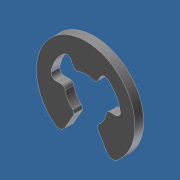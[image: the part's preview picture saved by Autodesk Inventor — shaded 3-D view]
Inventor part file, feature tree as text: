
AUTODESK INVENTOR PART (.ipt)
format: ipt  version: 2012 (Build 160160000, 160)  size: 113,152 bytes
history: native  units: in
note: dims shown in document units (in); Inventor stores cm internally (conversion verified against a paired STEP export)
features: other x7, extrude x1, sketch x1
ambient origin geometry x8: Origin, YZ Plane, XZ Plane, XY Plane, X Axis, Y Axis, Z Axis, Center Point
bodies: Solid1 (feature_tree)
feature tree (9):
  extrude  "Extrusion1"  [1 undecoded]
  other  "RR_XY"
  other  "RR_YZ"
  other  "RR_ZX"
  other  "RR_X"
  other  "RR_Y"
  other  "RR_Z"
  other  "RR_Center"
  sketch  "Sketch_1"  dims[d0=0.0435in d1=0.0in]
note: 1 required parameter value undecoded (feature->parameter linkage not recoverable at this tier; creation-order binding heuristic only, values carry confidence <= 0.55)
